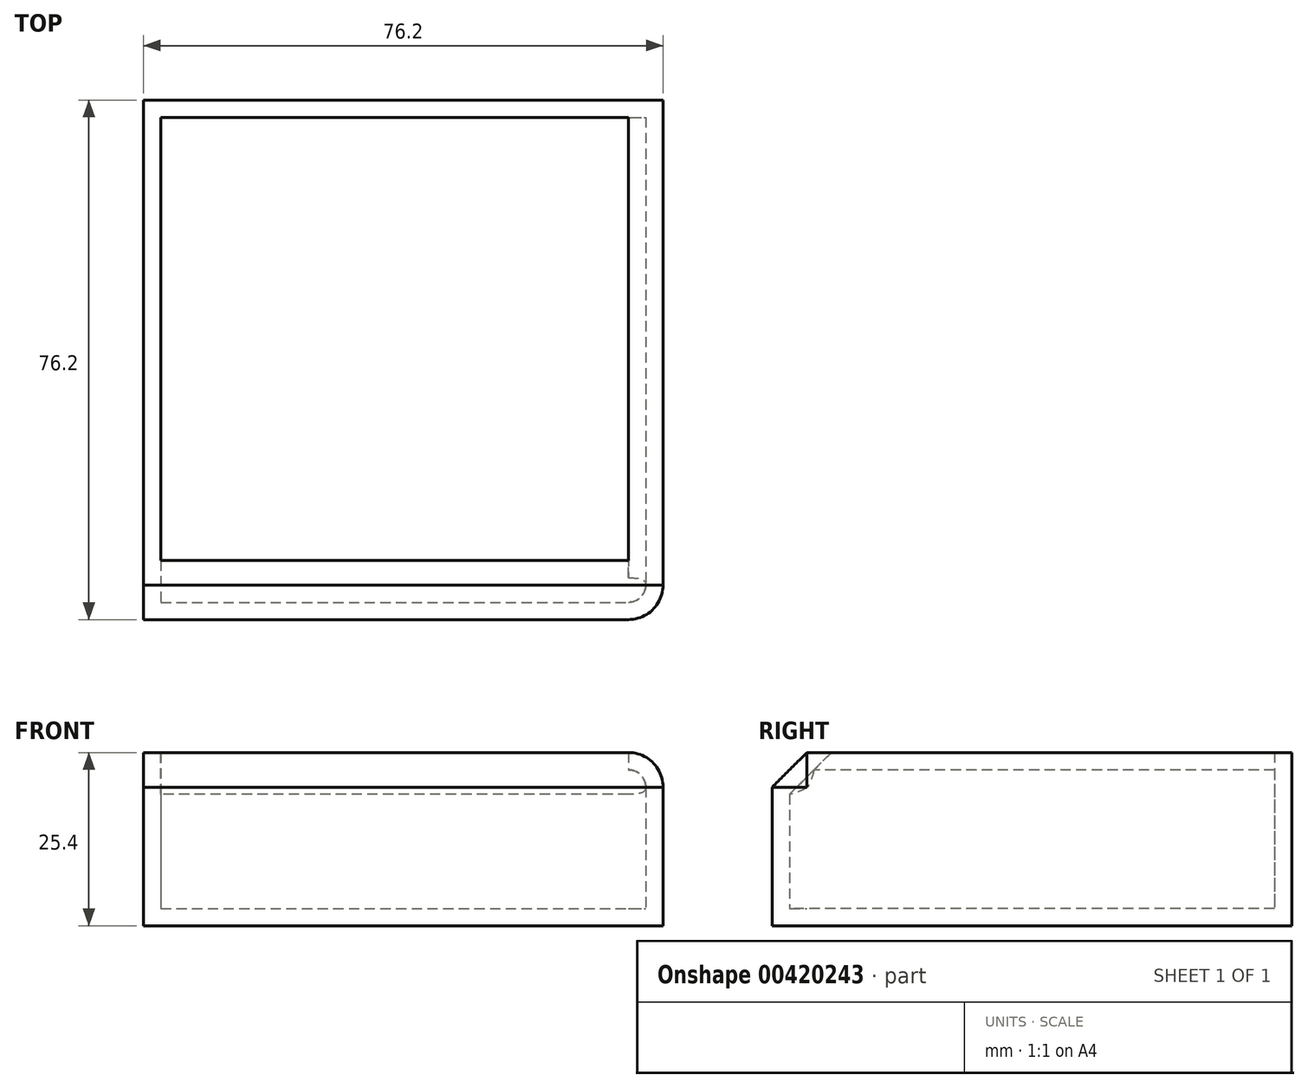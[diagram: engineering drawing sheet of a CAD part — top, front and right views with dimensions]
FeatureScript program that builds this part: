
annotation { "Feature Type Name" : "Feature", "Feature Type Description" : "" }
export const myFeature = defineFeature(function(context is Context, id is Id, definition is map)
    precondition{}
    {
        {
            var Q0;
            Q0=qCreatedBy(makeId("Top.planeOp"),FACE);
            var sketch = newSketch(context, id + "F0", { "sketchPlane" : qUnion([Q0])});
            skLineSegment(sketch, "E0.bottom", {"start": v(0, 0) * mm, "end": v(76.2, 0) * mm});
            skLineSegment(sketch, "E0.top", {"start": v(0, -76.2) * mm, "end": v(76.2, -76.2) * mm});
            skLineSegment(sketch, "E0.left", {"start": v(0, 0) * mm, "end": v(0, -76.2) * mm});
            skLineSegment(sketch, "E0.right", {"start": v(76.2, 0) * mm, "end": v(76.2, -76.2) * mm});
            skSolve(sketch);
        }
        {
            var Q0;
            Q0 = qSketchRegion(id + "F0", true);
            extrude(context, id + "F1", {"entities" : qUnion([Q0]), "depth" : 25.4 * mm});
        }
        {
            var Q0;
            Q0=makeQuery(id+"F1.opExtrude","SWEPT_EDGE",EDGE,{"disambiguationData":[OSD([sQuery(id+"F0.wireOp",EDGE,"E0.top"),sQuery(id+"F0.wireOp",EDGE,"E0.right")])]});
            var Q1;
            Q1=makeQuery(id+"F1.opExtrude","CAP_EDGE",EDGE,{"disambiguationData":[OSD([sQuery(id+"F0.wireOp",EDGE,"E0.right")])],"isStart":false});
            fillet(context, id + "F2", {"entities" : qUnion([Q0, Q1]), "radius" : 5.08 * mm, "tangentPropagation" : true, "allowEdgeOverflow" : false});
        }
        {
            var Q0;
            Q0=makeQuery(id+"F1.opExtrude","CAP_EDGE",EDGE,{"disambiguationData":[OSD([sQuery(id+"F0.wireOp",EDGE,"E0.top")])],"isStart":false});
            chamfer(context, id + "F3", {"entities" : qUnion([Q0]), "width" : 5.08 * mm, "tangentPropagation" : true});
        }
        {
            var Q0;
            Q0=makeQuery(id+"F1.opExtrude","CAP_FACE",FACE,{"disambiguationData":[OSD([sQuery(id+"F0.wireOp",EDGE,"E0.bottom"),sQuery(id+"F0.wireOp",EDGE,"E0.top"),sQuery(id+"F0.wireOp",EDGE,"E0.left"),sQuery(id+"F0.wireOp",EDGE,"E0.right")])],"isStart":false});
            shell(context, id + "F4", {"entities" : qUnion([Q0]), "thickness" : 2.54 * mm});
        }
    });
